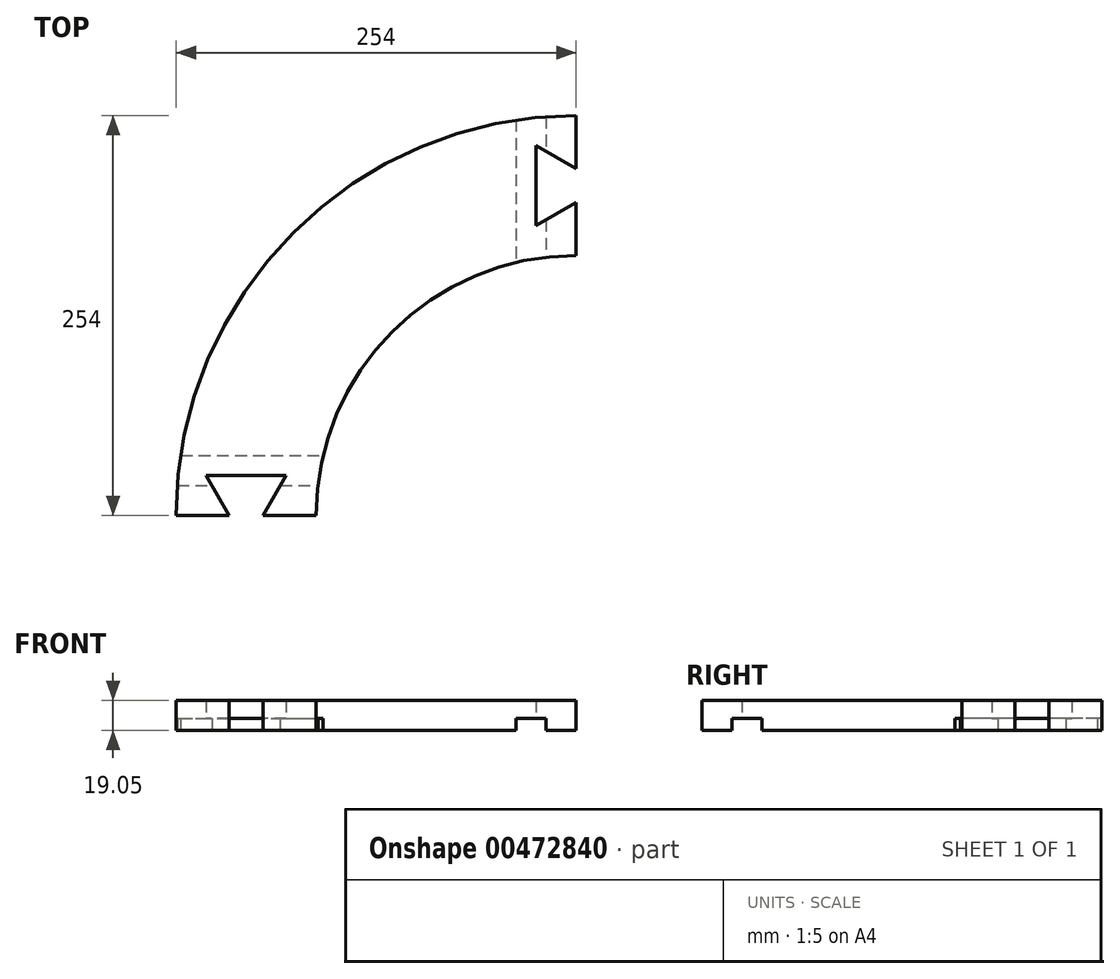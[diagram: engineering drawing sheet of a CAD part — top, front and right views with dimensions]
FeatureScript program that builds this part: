
annotation { "Feature Type Name" : "Feature", "Feature Type Description" : "" }
export const myFeature = defineFeature(function(context is Context, id is Id, definition is map)
    precondition{}
    {
        {
            var Q0;
            Q0=qCreatedBy(makeId("Top.planeOp"),FACE);
            var sketch = newSketch(context, id + "F0", { "sketchPlane" : qUnion([Q0])});
            skArc(sketch, "E0", {"start": v(-254, 0) * mm, "mid": v(-179.6, 179.6) * mm, "end": v(0, 254) * mm});
            skArc(sketch, "E1.0", {"start": v(-165.1, 0) * mm, "mid": v(-116.74, 116.74) * mm, "end": v(0, 165.1) * mm});
            skLineSegment(sketch, "E2", {"start": v(-254, 0) * mm, "end": v(-220.29, 0) * mm});
            skLineSegment(sketch, "E3", {"start": v(0, 254) * mm, "end": v(0, 220.29) * mm});
            skLineSegment(sketch, "E4", {"start": v(-220.29, 0) * mm, "end": v(-234.95, 25.4) * mm});
            skLineSegment(sketch, "E5", {"start": v(-234.95, 25.4) * mm, "end": v(-184.15, 25.4) * mm});
            skLineSegment(sketch, "E6", {"start": v(-184.15, 25.4) * mm, "end": v(-198.81, 0) * mm});
            skLineSegment(sketch, "E7.trimOffspring", {"start": v(-198.81, 0) * mm, "end": v(-165.1, 0) * mm});
            skLineSegment(sketch, "E8", {"start": v(0, 220.29) * mm, "end": v(-25.4, 234.95) * mm});
            skLineSegment(sketch, "E9", {"start": v(-25.4, 234.95) * mm, "end": v(-25.4, 184.15) * mm});
            skLineSegment(sketch, "E10", {"start": v(-25.4, 184.15) * mm, "end": v(0, 198.81) * mm});
            skLineSegment(sketch, "E11.trimOffspring", {"start": v(0, 198.81) * mm, "end": v(0, 165.1) * mm});
            skSolve(sketch);
        }
        {
            var Q0;
            Q0 = qSketchRegion(id + "F0", true);
            extrude(context, id + "F1", {"entities" : qUnion([Q0]), "depth" : 19.05 * mm});
        }
        {
            var Q0;
            Q0=qCreatedBy(makeId("Right.planeOp"),FACE);
            var sketch = newSketch(context, id + "F2", { "sketchPlane" : qUnion([Q0])});
            skLineSegment(sketch, "E12.bottom", {"start": v(19.05, 0) * mm, "end": v(38.1, 0) * mm});
            skLineSegment(sketch, "E12.top", {"start": v(19.05, 7.62) * mm, "end": v(38.1, 7.62) * mm});
            skLineSegment(sketch, "E12.left", {"start": v(19.05, 0) * mm, "end": v(19.05, 7.62) * mm});
            skLineSegment(sketch, "E12.right", {"start": v(38.1, 0) * mm, "end": v(38.1, 7.62) * mm});
            skSolve(sketch);
        }
        {
            var Q0;
            Q0 = qSketchRegion(id + "F2", true);
            extrude(context, id + "F3", {"entities" : qUnion([Q0]), "operationType" : NewBodyOperationType.REMOVE, "endBound" : BoundingType.THROUGH_ALL, "oppositeDirection" : true, "depth" : 25.4 * mm});
        }
        {
            var Q0;
            Q0=qCreatedBy(makeId("Front.planeOp"),FACE);
            var sketch = newSketch(context, id + "F4", { "sketchPlane" : qUnion([Q0])});
            skLineSegment(sketch, "E13.bottom", {"start": v(-19.05, 0) * mm, "end": v(-38.1, 0) * mm});
            skLineSegment(sketch, "E13.top", {"start": v(-19.05, 7.62) * mm, "end": v(-38.1, 7.62) * mm});
            skLineSegment(sketch, "E13.left", {"start": v(-19.05, 0) * mm, "end": v(-19.05, 7.62) * mm});
            skLineSegment(sketch, "E13.right", {"start": v(-38.1, 0) * mm, "end": v(-38.1, 7.62) * mm});
            skSolve(sketch);
        }
        {
            var Q0;
            Q0 = qSketchRegion(id + "F4", true);
            extrude(context, id + "F5", {"entities" : qUnion([Q0]), "operationType" : NewBodyOperationType.REMOVE, "endBound" : BoundingType.THROUGH_ALL, "oppositeDirection" : true, "depth" : 25.4 * mm});
        }
    });
